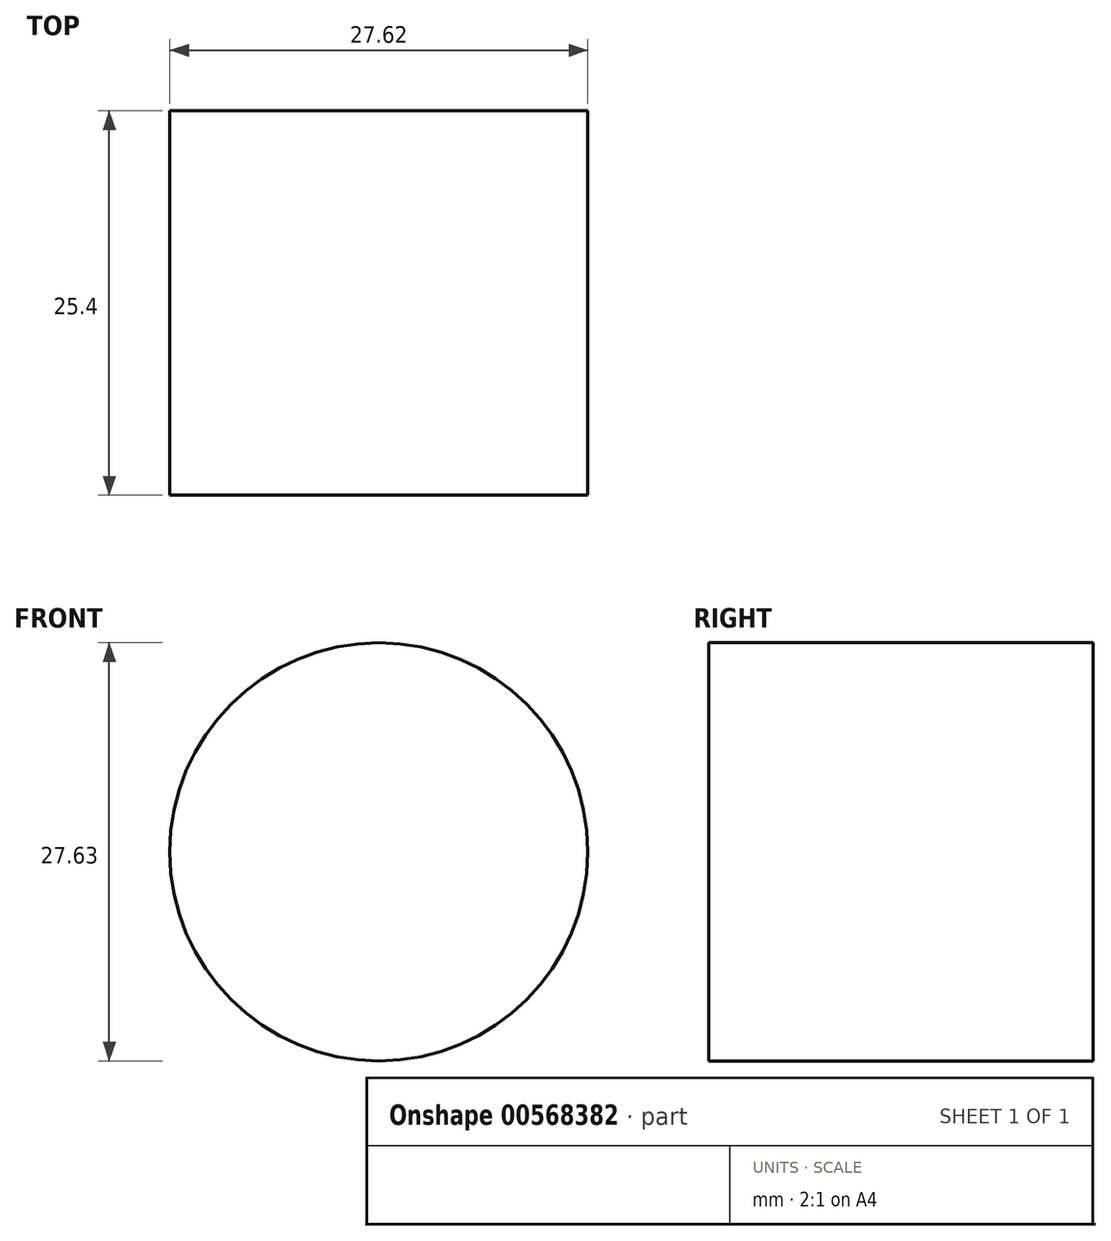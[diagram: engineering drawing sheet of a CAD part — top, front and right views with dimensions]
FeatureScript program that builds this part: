
annotation { "Feature Type Name" : "Feature", "Feature Type Description" : "" }
export const myFeature = defineFeature(function(context is Context, id is Id, definition is map)
    precondition{}
    {
        {
            var Q0;
            Q0=qCreatedBy(makeId("Front.planeOp"),FACE);
            var sketch = newSketch(context, id + "F0", { "sketchPlane" : qUnion([Q0])});
            skCircle(sketch, "E0", {"center": v(0, 61.94) * mm, "radius": 13.81 * mm});
            skLineSegment(sketch, "E1.bottom", {"start": v(0, 48.12) * mm, "end": v(-5.3, 48.12) * mm});
            skLineSegment(sketch, "E1.top", {"start": v(0, 4.1) * mm, "end": v(-5.3, 4.1) * mm});
            skLineSegment(sketch, "E1.left", {"start": v(0, 48.12) * mm, "end": v(0, 4.1) * mm});
            skLineSegment(sketch, "E1.right", {"start": v(-5.3, 48.12) * mm, "end": v(-5.3, 4.1) * mm});
            skLineSegment(sketch, "E2.bottom", {"start": v(0, 48.12) * mm, "end": v(7.95, 48.12) * mm});
            skLineSegment(sketch, "E2.top", {"start": v(0, 4.1) * mm, "end": v(7.95, 4.1) * mm});
            skLineSegment(sketch, "E2.right", {"start": v(7.95, 48.12) * mm, "end": v(7.95, 4.1) * mm});
            skLineSegment(sketch, "E3.bottom", {"start": v(-5.3, 48.12) * mm, "end": v(-12.77, 48.12) * mm});
            skLineSegment(sketch, "E3.top", {"start": v(-5.3, 40.73) * mm, "end": v(-12.77, 40.73) * mm});
            skLineSegment(sketch, "E3.left", {"start": v(-5.3, 48.12) * mm, "end": v(-5.3, 40.73) * mm});
            skLineSegment(sketch, "E3.right", {"start": v(-12.77, 48.12) * mm, "end": v(-12.77, 40.73) * mm});
            skLineSegment(sketch, "E4.bottom", {"start": v(7.95, 48.12) * mm, "end": v(14.46, 48.12) * mm});
            skLineSegment(sketch, "E4.top", {"start": v(7.95, 40.97) * mm, "end": v(14.46, 40.97) * mm});
            skLineSegment(sketch, "E4.left", {"start": v(7.95, 48.12) * mm, "end": v(7.95, 40.97) * mm});
            skLineSegment(sketch, "E4.right", {"start": v(14.46, 48.12) * mm, "end": v(14.46, 40.97) * mm});
            skLineSegment(sketch, "E5.bottom", {"start": v(-5.3, 4.1) * mm, "end": v(0, 4.1) * mm});
            skLineSegment(sketch, "E5.top", {"start": v(-5.3, -21.93) * mm, "end": v(0, -21.93) * mm});
            skLineSegment(sketch, "E5.left", {"start": v(-5.3, 4.1) * mm, "end": v(-5.3, -21.93) * mm});
            skLineSegment(sketch, "E5.right", {"start": v(0, 4.1) * mm, "end": v(0, -21.93) * mm});
            skLineSegment(sketch, "E6.top", {"start": v(0, -21.69) * mm, "end": v(7.95, -21.69) * mm});
            skLineSegment(sketch, "E6.left", {"start": v(0, 4.1) * mm, "end": v(0, -21.69) * mm});
            skLineSegment(sketch, "E6.right", {"start": v(7.95, 4.1) * mm, "end": v(7.95, -21.69) * mm});
            skSolve(sketch);
        }
        {
            var Q0;
            Q0=makeQuery(id+"F0.imprint","IMPRINT",FACE,{"disambiguationData":[TD([[makeQuery(id+"F0.imprint","IMPRINT",EDGE,{"derivedFrom":sQuery(id+"F0.wireOp",EDGE,"E0")}),1.0]])]});
            extrude(context, id + "F1", {"entities" : qUnion([Q0]), "depth" : 25.4 * mm, "offsetDistance" : 25.4 * mm});
        }
    });
